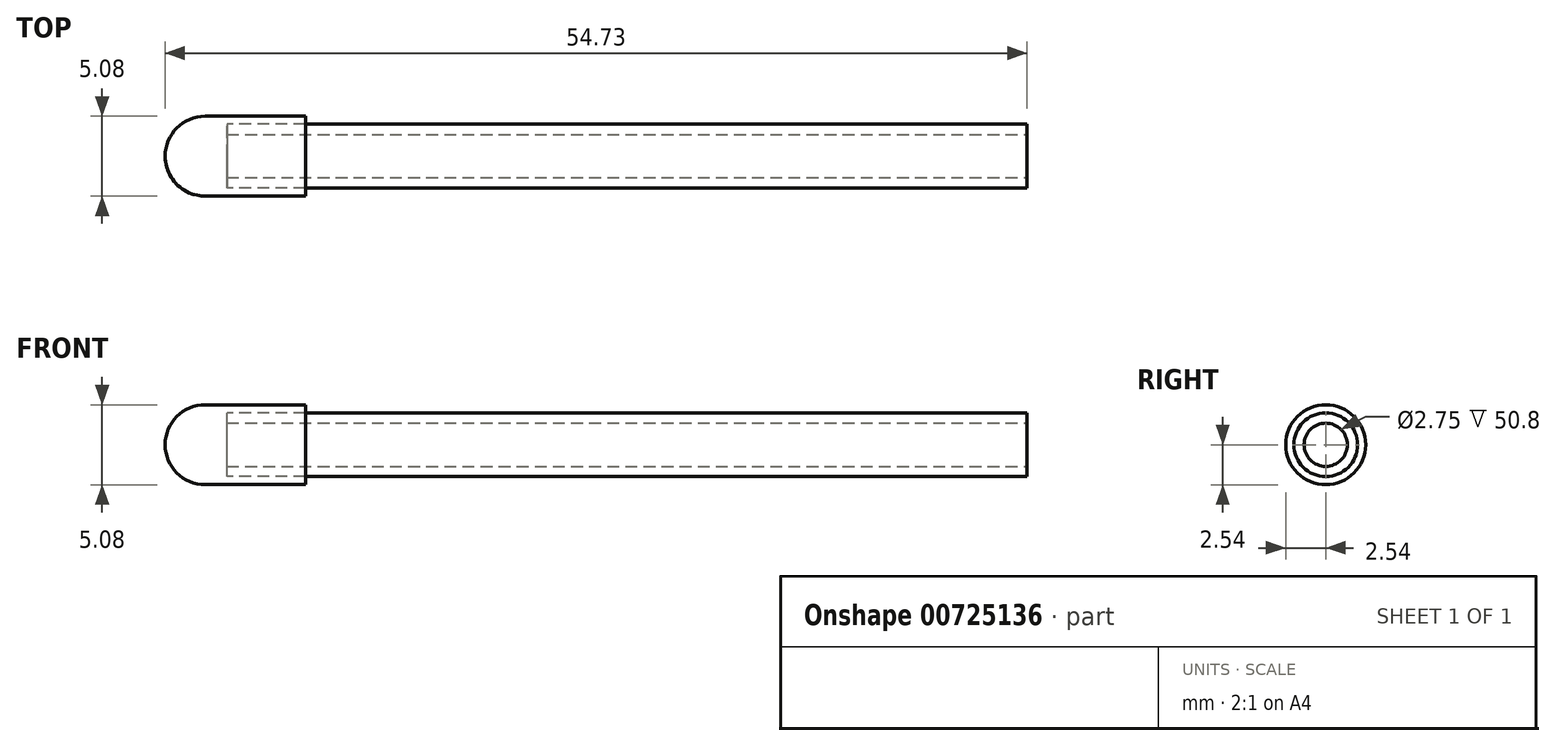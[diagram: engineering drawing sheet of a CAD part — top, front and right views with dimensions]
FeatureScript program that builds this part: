
annotation { "Feature Type Name" : "Feature", "Feature Type Description" : "" }
export const myFeature = defineFeature(function(context is Context, id is Id, definition is map)
    precondition{}
    {
        {
            var Q0;
            Q0=qCreatedBy(makeId("Right.planeOp"),FACE);
            var sketch = newSketch(context, id + "F0", { "sketchPlane" : qUnion([Q0])});
            skCircle(sketch, "E0", {"center": v(0, 0) * mm, "radius": 2.03 * mm});
            skSolve(sketch);
        }
        {
            var Q0;
            Q0 = qSketchRegion(id + "F0", true);
            extrude(context, id + "F1", {"entities" : qUnion([Q0]), "depth" : 50.8 * mm, "offsetDistance" : 25.4 * mm, "symmetric" : true});
        }
        {
            var Q0;
            Q0=qCreatedBy(makeId("Right.planeOp"),FACE);
            var sketch = newSketch(context, id + "F2", { "sketchPlane" : qUnion([Q0])});
            skCircle(sketch, "E1", {"center": v(0, 0) * mm, "radius": 1.37 * mm});
            skSolve(sketch);
        }
        {
            var Q0;
            Q0 = qSketchRegion(id + "F2", true);
            extrude(context, id + "F3", {"entities" : qUnion([Q0]), "operationType" : NewBodyOperationType.REMOVE, "oppositeDirection" : true, "depth" : 50.8 * mm, "offsetDistance" : 25.4 * mm, "symmetric" : true});
        }
        {
            var Q0;
            Q0=qCreatedBy(makeId("Top.planeOp"),FACE);
            var sketch = newSketch(context, id + "F4", { "sketchPlane" : qUnion([Q0])});
            skLineSegment(sketch, "E2", {"start": v(0, 0) * mm, "end": v(-29.33, 0) * mm});
            skArc(sketch, "E3", {"start": v(-29.33, 0) * mm, "mid": v(-28.59, -1.8) * mm, "end": v(-26.8, -2.54) * mm});
            skLineSegment(sketch, "E4", {"start": v(-26.8, -2.54) * mm, "end": v(-20.43, -2.54) * mm});
            skLineSegment(sketch, "E5", {"start": v(-20.43, -2.54) * mm, "end": v(-20.43, 0) * mm});
            skLineSegment(sketch, "E6", {"start": v(-20.43, 0) * mm, "end": v(-29.33, 0) * mm});
            skSolve(sketch);
        }
        {
            var Q0;
            Q0=makeQuery(id+"F4.imprint","IMPRINT",FACE,{"disambiguationData":[TD([[makeQuery(id+"F4.imprint","IMPRINT",EDGE,{"derivedFrom":sQuery(id+"F4.wireOp",EDGE,"E3")}),1.0]])]});
            var Q1;
            Q1=sQuery(id+"F4.wireOp",EDGE,"E2");
            revolve(context, id + "F5", {"surfaceOperationType" : NewSurfaceOperationType.NEW, "entities" : qUnion([Q0]), "axis" : qUnion([Q1]), "revolveType" : RevolveType.FULL});
        }
    });
